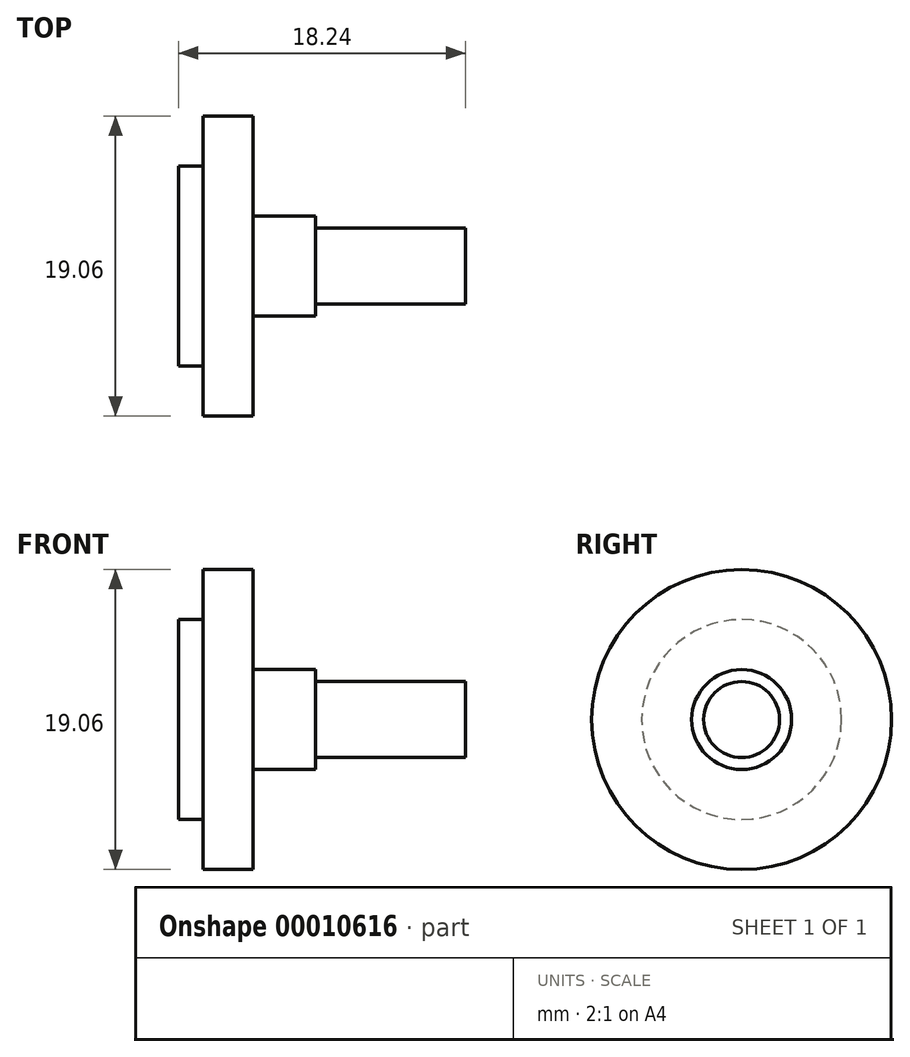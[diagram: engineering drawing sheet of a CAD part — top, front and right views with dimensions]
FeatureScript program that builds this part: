
annotation { "Feature Type Name" : "Feature", "Feature Type Description" : "" }
export const myFeature = defineFeature(function(context is Context, id is Id, definition is map)
    precondition{}
    {
        {
            var Q0;
            Q0=qCreatedBy(makeId("Right.planeOp"),FACE);
            var sketch = newSketch(context, id + "F0", { "sketchPlane" : qUnion([Q0])});
            skCircle(sketch, "E0", {"center": v(0, 0) * mm, "radius": 9.53 * mm});
            skCircle(sketch, "E1", {"center": v(0, 0) * mm, "radius": 6.35 * mm});
            skCircle(sketch, "E2", {"center": v(0, 0) * mm, "radius": 3.18 * mm});
            skCircle(sketch, "E3", {"center": v(0, 0) * mm, "radius": 2.41 * mm});
            skSolve(sketch);
        }
        {
            var Q0;
            Q0=makeQuery(id+"F0.imprint","IMPRINT",FACE,{"disambiguationData":[TD([[makeQuery(id+"F0.imprint","IMPRINT",EDGE,{"derivedFrom":sQuery(id+"F0.wireOp",EDGE,"E1")}),1.0]])]});
            var Q1;
            Q1=makeQuery(id+"F0.imprint","IMPRINT",FACE,{"disambiguationData":[TD([[makeQuery(id+"F0.imprint","IMPRINT",EDGE,{"derivedFrom":sQuery(id+"F0.wireOp",EDGE,"E3")}),1.0]])]});
            var Q2;
            Q2=makeQuery(id+"F0.imprint","IMPRINT",FACE,{"disambiguationData":[TD([[makeQuery(id+"F0.imprint","IMPRINT",EDGE,{"derivedFrom":sQuery(id+"F0.wireOp",EDGE,"E2")}),1.0]])]});
            extrude(context, id + "F1", {"entities" : qUnion([Q0, Q1, Q2]), "depth" : 1.57 * mm});
        }
        {
            var Q0;
            Q0=makeQuery(id+"F1.opExtrude","CAP_FACE",FACE,{"disambiguationData":[OSD([sQuery(id+"F0.wireOp",EDGE,"E1"),sQuery(id+"F0.wireOp",EDGE,"E2")])],"isStart":false});
            var sketch = newSketch(context, id + "F2", { "sketchPlane" : qUnion([Q0])});
            skCircle(sketch, "E4.0", {"center": v(0, 0) * mm, "radius": 9.53 * mm});
            skSolve(sketch);
        }
        {
            var Q0;
            Q0=qSketchRegion(id+"F2",true);
            extrude(context, id + "F3", {"entities" : qUnion([Q0]), "operationType" : NewBodyOperationType.ADD, "depth" : 3.17 * mm});
        }
        {
            var Q0;
            Q0=makeQuery(id+"F3.opExtrude","CAP_FACE",FACE,{"disambiguationData":[OSD([sQuery(id+"F2.wireOp",EDGE,"E4.0")])],"isStart":false});
            var sketch = newSketch(context, id + "F4", { "sketchPlane" : qUnion([Q0])});
            skCircle(sketch, "E5.0", {"center": v(0, 0) * mm, "radius": 3.18 * mm});
            skSolve(sketch);
        }
        {
            var Q0;
            Q0=qSketchRegion(id+"F4",true);
            extrude(context, id + "F5", {"entities" : qUnion([Q0]), "operationType" : NewBodyOperationType.ADD, "depth" : 3.96 * mm});
        }
        {
            var Q0;
            Q0=makeQuery(id+"F5.opExtrude","CAP_FACE",FACE,{"disambiguationData":[OSD([sQuery(id+"F4.wireOp",EDGE,"E5.0")])],"isStart":false});
            var sketch = newSketch(context, id + "F6", { "sketchPlane" : qUnion([Q0])});
            skCircle(sketch, "E6.0", {"center": v(0, 0) * mm, "radius": 2.41 * mm});
            skSolve(sketch);
        }
        {
            var Q0;
            Q0=qSketchRegion(id+"F6",true);
            extrude(context, id + "F7", {"entities" : qUnion([Q0]), "operationType" : NewBodyOperationType.ADD, "depth" : 9.52 * mm});
        }
    });
